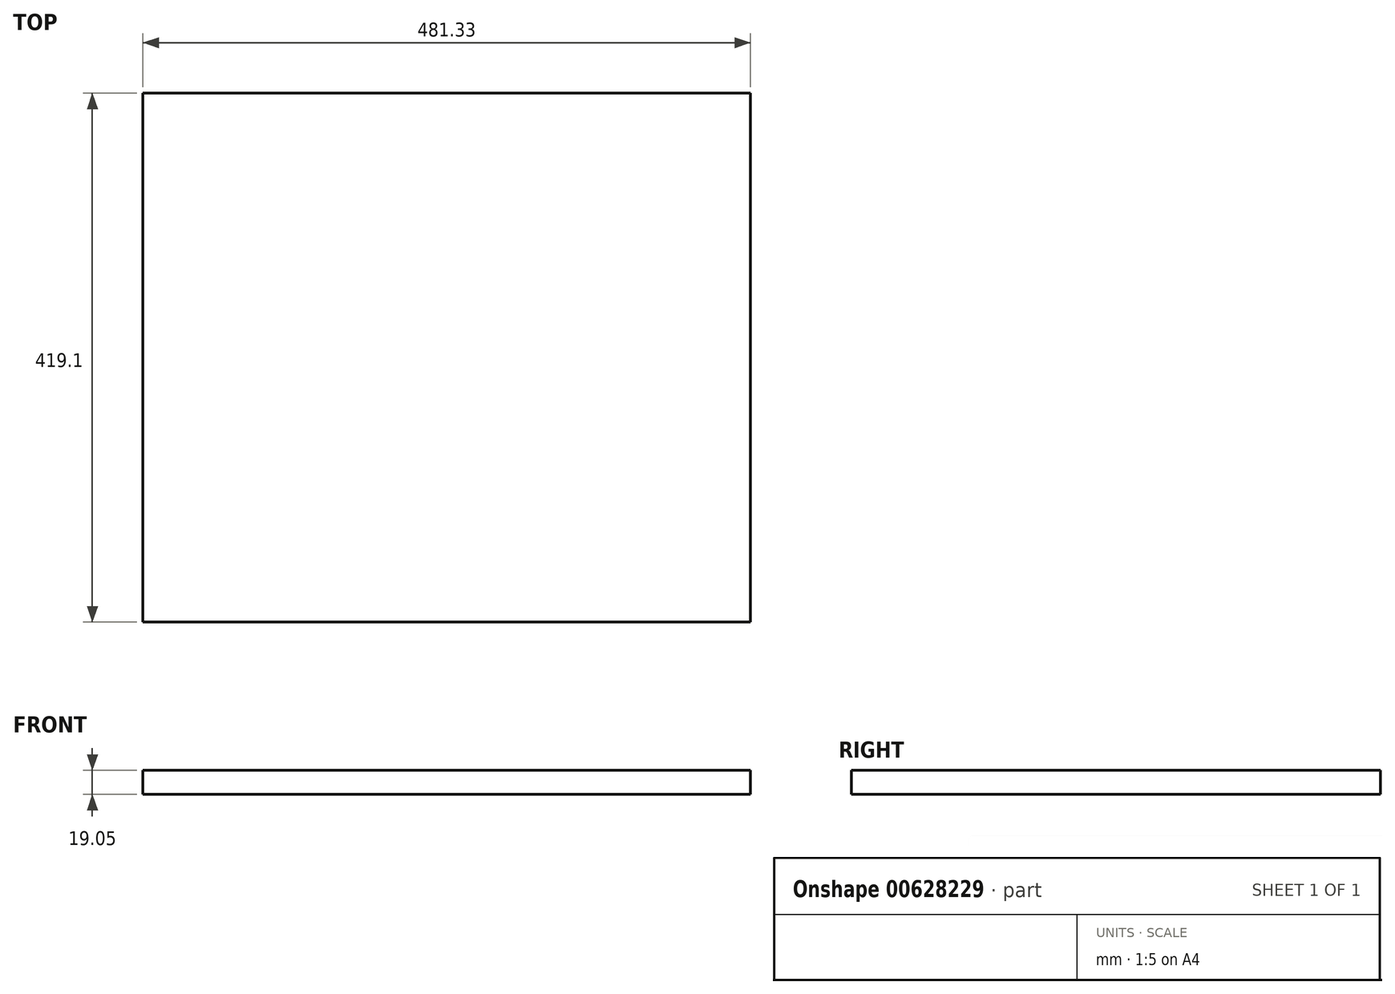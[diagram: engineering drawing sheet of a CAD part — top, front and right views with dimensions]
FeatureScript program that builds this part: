
annotation { "Feature Type Name" : "Feature", "Feature Type Description" : "" }
export const myFeature = defineFeature(function(context is Context, id is Id, definition is map)
    precondition{}
    {
        {
            var Q0;
            Q0=qCreatedBy(makeId("Top.planeOp"),FACE);
            var sketch = newSketch(context, id + "F0", { "sketchPlane" : qUnion([Q0])});
            skLineSegment(sketch, "E0.bottom", {"start": v(0, 0) * mm, "end": v(481.33, 0) * mm});
            skLineSegment(sketch, "E0.top", {"start": v(0, 419.1) * mm, "end": v(481.33, 419.1) * mm});
            skLineSegment(sketch, "E0.left", {"start": v(0, 0) * mm, "end": v(0, 419.1) * mm});
            skLineSegment(sketch, "E0.right", {"start": v(481.33, 0) * mm, "end": v(481.33, 419.1) * mm});
            skSolve(sketch);
        }
        {
            var Q0;
            Q0=makeQuery(id+"F0.imprint","IMPRINT",FACE,{"disambiguationData":[TD([[makeQuery(id+"F0.imprint","IMPRINT",EDGE,{"derivedFrom":sQuery(id+"F0.wireOp",EDGE,"E0.bottom")}),1.0]])]});
            extrude(context, id + "F1", {"entities" : qUnion([Q0]), "depth" : 19.05 * mm, "offsetDistance" : 25.4 * mm});
        }
    });
